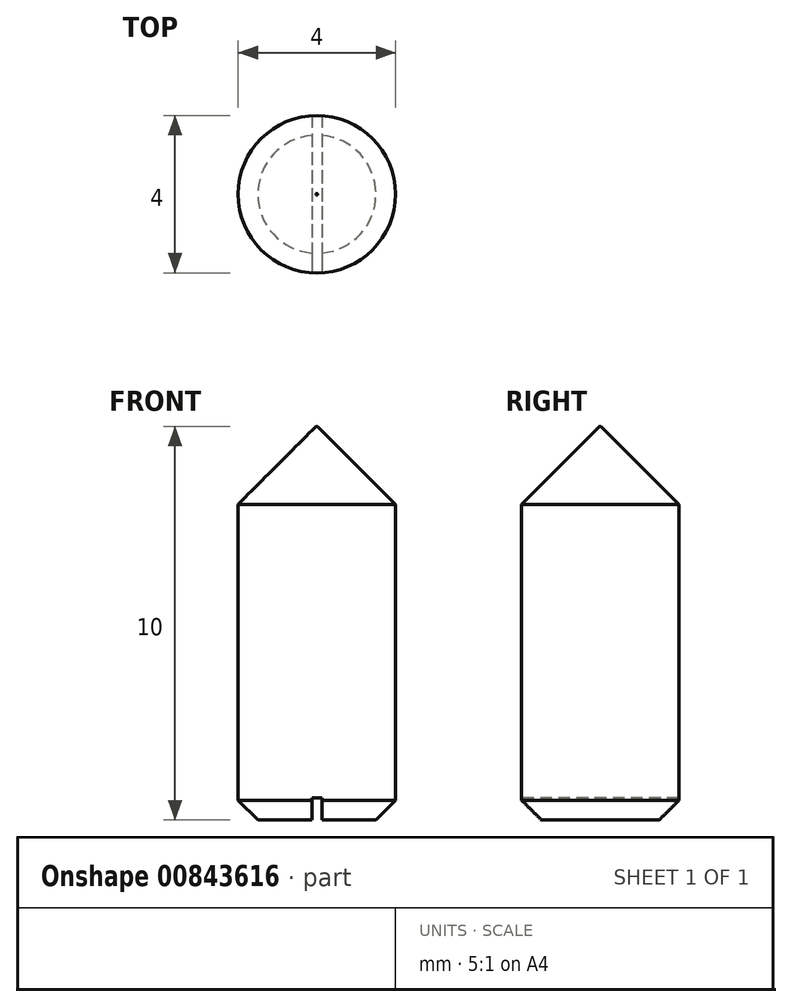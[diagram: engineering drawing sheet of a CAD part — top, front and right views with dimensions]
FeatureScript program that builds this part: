
annotation { "Feature Type Name" : "Feature", "Feature Type Description" : "" }
export const myFeature = defineFeature(function(context is Context, id is Id, definition is map)
    precondition{}
    {
        {
            var Q0;
            Q0=qCreatedBy(makeId("Top.planeOp"),FACE);
            var sketch = newSketch(context, id + "F0", { "sketchPlane" : qUnion([Q0])});
            skCircle(sketch, "E0", {"center": v(0, 0) * mm, "radius": 2 * mm});
            skSolve(sketch);
        }
        {
            var Q0;
            Q0 = qSketchRegion(id + "F0", true);
            extrude(context, id + "F1", {"entities" : qUnion([Q0]), "depth" : 10 * mm, "offsetDistance" : 25 * mm});
        }
        {
            var Q0;
            Q0=qCreatedBy(makeId("Right.planeOp"),FACE);
            var sketch = newSketch(context, id + "F2", { "sketchPlane" : qUnion([Q0])});
            skLineSegment(sketch, "E1", {"start": v(-2.46, 10.2) * mm, "end": v(0, 10.2) * mm});
            skLineSegment(sketch, "E2", {"start": v(0, 10.02) * mm, "end": v(-2.46, 7.56) * mm});
            skLineSegment(sketch, "E3", {"start": v(-2.46, 10.2) * mm, "end": v(-2.46, 7.56) * mm});
            skLineSegment(sketch, "E4", {"start": v(0, 10.2) * mm, "end": v(0, 10.02) * mm});
            skSolve(sketch);
        }
        {
            var Q0;
            Q0=makeQuery(id+"F2.imprint","IMPRINT",FACE,{"disambiguationData":[TD([[makeQuery(id+"F2.imprint","IMPRINT",EDGE,{"derivedFrom":sQuery(id+"F2.wireOp",EDGE,"E1")}),-1.0]])]});
            var Q1;
            Q1=sQuery(id+"F2.wireOp",EDGE,"E4");
            revolve(context, id + "F3", {"operationType" : NewBodyOperationType.REMOVE, "surfaceOperationType" : NewSurfaceOperationType.NEW, "entities" : qUnion([Q0]), "axis" : qUnion([Q1]), "revolveType" : RevolveType.FULL, "oppositeDirection" : true});
        }
        {
            var Q0;
            Q0=makeQuery(id+"F1.opExtrude","CAP_EDGE",EDGE,{"disambiguationData":[OSD([sQuery(id+"F0.wireOp",EDGE,"E0")])],"isStart":true});
            chamfer(context, id + "F4", {"entities" : qUnion([Q0]), "width" : .5 * mm, "tangentPropagation" : true});
        }
        {
            var Q0;
            Q0=makeQuery(id+"F1.opExtrude","CAP_FACE",FACE,{"disambiguationData":[OSD([sQuery(id+"F0.wireOp",EDGE,"E0")])],"isStart":true});
            var sketch = newSketch(context, id + "F5", { "sketchPlane" : qUnion([Q0])});
            skLineSegment(sketch, "E5.bottom", {"start": v(0.12, -2.36) * mm, "end": v(-0.12, -2.36) * mm});
            skLineSegment(sketch, "E5.top", {"start": v(0.12, 2.36) * mm, "end": v(-0.12, 2.36) * mm});
            skLineSegment(sketch, "E5.left", {"start": v(0.12, -2.36) * mm, "end": v(0.12, 2.36) * mm});
            skLineSegment(sketch, "E5.right", {"start": v(-0.12, -2.36) * mm, "end": v(-0.12, 2.36) * mm});
            skPoint(sketch, "E5.middle", {"position": v(0, 0) * mm});
            skSolve(sketch);
        }
        {
            var Q0;
            {var subQ0=sQuery(id+"F5.wireOp",EDGE,"E5.top");Q0=makeQuery(id+"F5.imprint","IMPRINT",FACE,{"disambiguationData":[TD([[makeQuery(id+"F5.imprint","IMPRINT",EDGE,{"derivedFrom":subQ0}),1.0]])]});}
            var Q1;
            {var subQ0=sQuery(id+"F5.wireOp",EDGE,"E5.left");var subQ1=sQuery(id+"F0.wireOp",EDGE,"E0");var subQ2=makeQuery(id+"F4.opChamfer","BLEND_EDGE",EDGE,{"blendedFrom":[makeQuery(id+"F1.opExtrude","CAP_EDGE",EDGE,{"disambiguationData":[OSD([subQ1])],"isStart":true}),makeQuery(id+"F1.opExtrude","CAP_FACE",FACE,{"disambiguationData":[OSD([subQ1])],"isStart":true})],"blendedInto":[makeQuery(id+"F1.opExtrude","CAP_FACE",FACE,{"disambiguationData":[OSD([subQ1])],"isStart":true})]});var subQ3=makeQuery(id+"F5.imprint","INTERSECT",VERTEX,{"disambiguationData":[OD(0.0)],"derivedFrom":[subQ2,subQ0]});Q1=makeQuery(id+"F5.imprint","IMPRINT",FACE,{"disambiguationData":[TD([[makeQuery(id+"F5.imprint","IMPRINT",EDGE,{"disambiguationData":[TD([[subQ3,-1.0]])],"derivedFrom":subQ0}),1.0]])]});}
            var Q2;
            {var subQ0=sQuery(id+"F5.wireOp",EDGE,"E5.bottom");Q2=makeQuery(id+"F5.imprint","IMPRINT",FACE,{"disambiguationData":[TD([[makeQuery(id+"F5.imprint","IMPRINT",EDGE,{"derivedFrom":subQ0}),-1.0]])]});}
            extrude(context, id + "F6", {"entities" : qUnion([Q0, Q1, Q2]), "operationType" : NewBodyOperationType.REMOVE, "oppositeDirection" : true, "depth" : .56 * mm, "offsetDistance" : 25 * mm});
        }
    });
